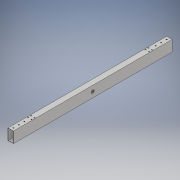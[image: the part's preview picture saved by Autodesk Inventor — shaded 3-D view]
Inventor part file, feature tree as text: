
AUTODESK INVENTOR PART (.ipt)
format: ipt  version: 2018 (Build 220112000, 112)  size: 166,912 bytes
history: native  units: in
note: dims shown in document units (in); Inventor stores cm internally (conversion verified against a paired STEP export)
features: extrude x4, sketch x4
ambient origin geometry x8: Origin, YZ Plane, XZ Plane, XY Plane, X Axis, Y Axis, Z Axis, Center Point
bodies: Solid1 (feature_tree)
feature tree (8):
  extrude  "Extrusion1"  Depth=2.0in
  extrude  "Extrusion4"  Depth=29.0in TaperAngle=0.0deg
  extrude  "Extrusion5"  Depth=1.0in
  extrude  "Extrusion6"  Depth=1.0in
  sketch  "Sketch1"  dims[d0=1.0in d1=2.0in]
  sketch  "Sketch4"  dims[d2=0.0625in d3=29.0in d4=0.0in]
  sketch  "Sketch5"  dims[d15=0.5in d16=1.0in]
  sketch  "Sketch6"  dims[d17=1.0in d18=0.2031in d19=6.0in d20=0.0in d21=1.0in d22=0.59in d23=1.0in d24=0.0in d26=3.5in d28=0.187in d29=0.6299in d30=0.5315in d31=0.1811in d33=14.5in d34=10.9375in d35=0.0in]
